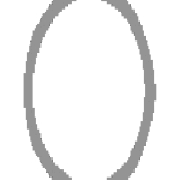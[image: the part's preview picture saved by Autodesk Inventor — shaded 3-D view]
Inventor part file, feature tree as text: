
AUTODESK INVENTOR PART (.ipt)
format: ipt  version: 2021 (Build 250183000, 183)  size: 112,640 bytes
history: native  units: in
note: dims shown in document units (in); Inventor stores cm internally (conversion verified against a paired STEP export)
features: other x4, sketch x3, plane x1
ambient origin geometry x8: Origin, YZ Plane, XZ Plane, XY Plane, X Axis, Y Axis, Z Axis, Center Point
bodies: Solid1 (feature_tree), Body (feature_tree)
feature tree (8):
  other  "Driven Length"
  other  "Frame Generator"
  other  "Start Plane"
  other  "End Plane"
  sketch  "Sketch"  dims[d2=8.0898in d4=-0.0in d5=8.0898in d6=0.12in d7=0.0in d8=90.0deg d9=8.0898in]
  sketch  "Sketch2"  dims[d0=1.0in]
  plane  "Work Plane3"
  sketch  "Sketch3"  dims[d1=0.065in]
